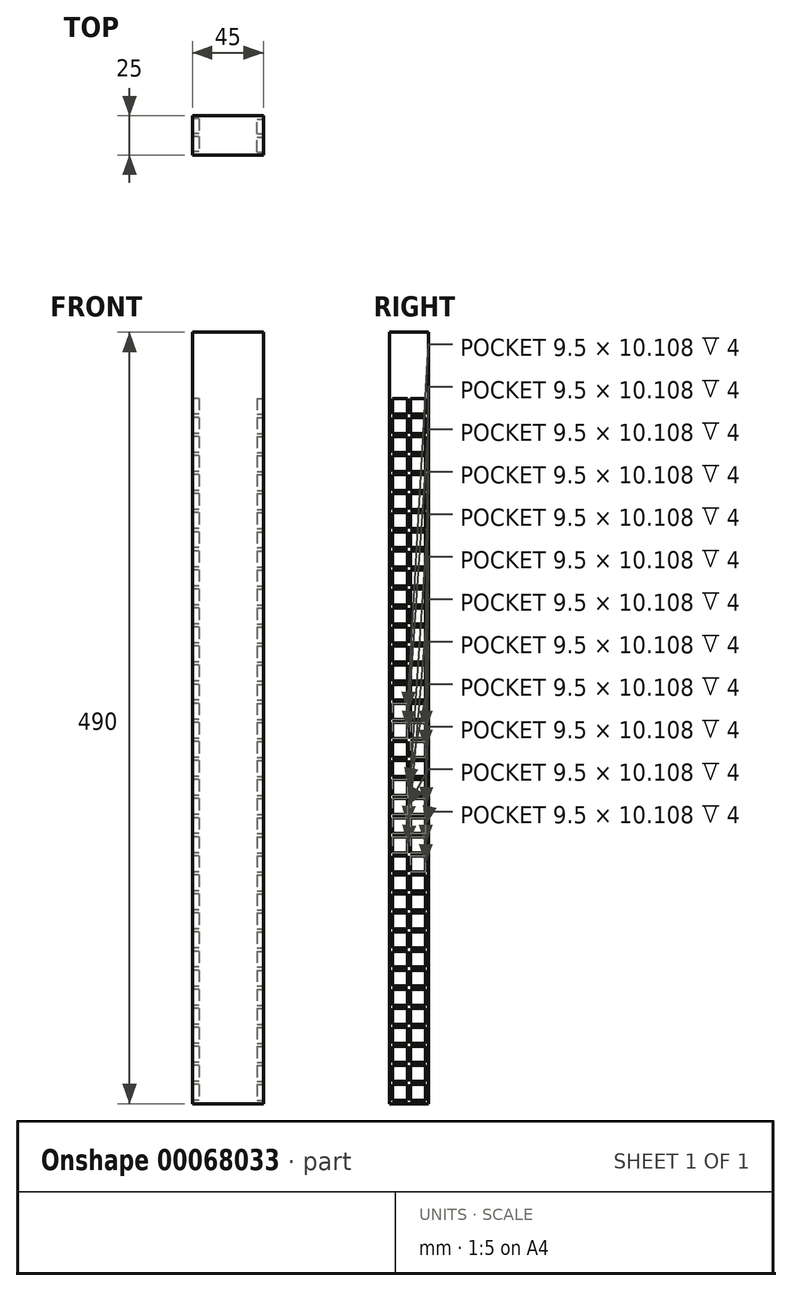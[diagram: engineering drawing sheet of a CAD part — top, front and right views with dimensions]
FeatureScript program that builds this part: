
annotation { "Feature Type Name" : "Feature", "Feature Type Description" : "" }
export const myFeature = defineFeature(function(context is Context, id is Id, definition is map)
    precondition{}
    {
        {
            var Q0;
            Q0=qCreatedBy(makeId("Top.planeOp"),FACE);
            var sketch = newSketch(context, id + "F0", { "sketchPlane" : qUnion([Q0])});
            skLineSegment(sketch, "E0.bottom", {"start": v(0, 0) * mm, "end": v(45, 0) * mm});
            skLineSegment(sketch, "E0.top", {"start": v(0, -25) * mm, "end": v(45, -25) * mm});
            skLineSegment(sketch, "E0.left", {"start": v(0, 0) * mm, "end": v(0, -25) * mm});
            skLineSegment(sketch, "E0.right", {"start": v(45, 0) * mm, "end": v(45, -25) * mm});
            skSolve(sketch);
        }
        {
            var Q0;
            Q0 = qSketchRegion(id + "F0", true);
            extrude(context, id + "F1", {"entities" : qUnion([Q0]), "depth" : 490 * mm});
        }
        {
            var Q0;
            Q0=makeQuery(id+"F1.opExtrude","SWEPT_FACE",FACE,{"disambiguationData":[OSD([sQuery(id+"F0.wireOp",EDGE,"E0.right")])]});
            var sketch = newSketch(context, id + "F2", { "sketchPlane" : qUnion([Q0])});
            skLineSegment(sketch, "E1.bottom", {"start": v(-23, 448) * mm, "end": v(-13.5, 448) * mm});
            skLineSegment(sketch, "E1.top", {"start": v(-23, 437.9) * mm, "end": v(-13.5, 437.9) * mm});
            skLineSegment(sketch, "E1.left", {"start": v(-23, 448) * mm, "end": v(-23, 437.9) * mm});
            skLineSegment(sketch, "E1.right", {"start": v(-13.5, 448) * mm, "end": v(-13.5, 437.9) * mm});
            skLineSegment(sketch, "E2.bottom", {"start": v(-11.5, 448) * mm, "end": v(-2, 448) * mm});
            skLineSegment(sketch, "E2.top", {"start": v(-11.5, 437.9) * mm, "end": v(-2, 437.9) * mm});
            skLineSegment(sketch, "E2.left", {"start": v(-11.5, 448) * mm, "end": v(-11.5, 437.9) * mm});
            skLineSegment(sketch, "E2.right", {"start": v(-2, 448) * mm, "end": v(-2, 437.9) * mm});
            skLineSegment(sketch, "E3.0.1.0", {"start": v(-2, 435.9) * mm, "end": v(-2, 425.78) * mm});
            skLineSegment(sketch, "E3.0.1.1", {"start": v(-11.5, 425.78) * mm, "end": v(-2, 425.78) * mm});
            skLineSegment(sketch, "E3.0.1.2", {"start": v(-23, 425.78) * mm, "end": v(-13.5, 425.78) * mm});
            skLineSegment(sketch, "E3.0.1.3", {"start": v(-23, 435.9) * mm, "end": v(-13.5, 435.9) * mm});
            skLineSegment(sketch, "E3.0.1.4", {"start": v(-23, 435.9) * mm, "end": v(-23, 425.78) * mm});
            skLineSegment(sketch, "E3.0.1.5", {"start": v(-13.5, 435.9) * mm, "end": v(-13.5, 425.78) * mm});
            skLineSegment(sketch, "E3.0.1.6", {"start": v(-11.5, 435.9) * mm, "end": v(-2, 435.9) * mm});
            skLineSegment(sketch, "E3.0.1.7", {"start": v(-11.5, 435.9) * mm, "end": v(-11.5, 425.78) * mm});
            skLineSegment(sketch, "E3.0.2.0", {"start": v(-2, 423.78) * mm, "end": v(-2, 413.68) * mm});
            skLineSegment(sketch, "E3.0.2.1", {"start": v(-11.5, 413.68) * mm, "end": v(-2, 413.68) * mm});
            skLineSegment(sketch, "E3.0.2.2", {"start": v(-23, 413.68) * mm, "end": v(-13.5, 413.68) * mm});
            skLineSegment(sketch, "E3.0.2.3", {"start": v(-23, 423.78) * mm, "end": v(-13.5, 423.78) * mm});
            skLineSegment(sketch, "E3.0.2.4", {"start": v(-23, 423.78) * mm, "end": v(-23, 413.68) * mm});
            skLineSegment(sketch, "E3.0.2.5", {"start": v(-13.5, 423.78) * mm, "end": v(-13.5, 413.68) * mm});
            skLineSegment(sketch, "E3.0.2.6", {"start": v(-11.5, 423.78) * mm, "end": v(-2, 423.78) * mm});
            skLineSegment(sketch, "E3.0.2.7", {"start": v(-11.5, 423.78) * mm, "end": v(-11.5, 413.68) * mm});
            skLineSegment(sketch, "E3.0.3.0", {"start": v(-2, 411.68) * mm, "end": v(-2, 401.57) * mm});
            skLineSegment(sketch, "E3.0.3.1", {"start": v(-11.5, 401.57) * mm, "end": v(-2, 401.57) * mm});
            skLineSegment(sketch, "E3.0.3.2", {"start": v(-23, 401.57) * mm, "end": v(-13.5, 401.57) * mm});
            skLineSegment(sketch, "E3.0.3.3", {"start": v(-23, 411.68) * mm, "end": v(-13.5, 411.68) * mm});
            skLineSegment(sketch, "E3.0.3.4", {"start": v(-23, 411.68) * mm, "end": v(-23, 401.57) * mm});
            skLineSegment(sketch, "E3.0.3.5", {"start": v(-13.5, 411.68) * mm, "end": v(-13.5, 401.57) * mm});
            skLineSegment(sketch, "E3.0.3.6", {"start": v(-11.5, 411.68) * mm, "end": v(-2, 411.68) * mm});
            skLineSegment(sketch, "E3.0.3.7", {"start": v(-11.5, 411.68) * mm, "end": v(-11.5, 401.57) * mm});
            skLineSegment(sketch, "E3.0.4.0", {"start": v(-2, 399.57) * mm, "end": v(-2, 389.46) * mm});
            skLineSegment(sketch, "E3.0.4.1", {"start": v(-11.5, 389.46) * mm, "end": v(-2, 389.46) * mm});
            skLineSegment(sketch, "E3.0.4.2", {"start": v(-23, 389.46) * mm, "end": v(-13.5, 389.46) * mm});
            skLineSegment(sketch, "E3.0.4.3", {"start": v(-23, 399.57) * mm, "end": v(-13.5, 399.57) * mm});
            skLineSegment(sketch, "E3.0.4.4", {"start": v(-23, 399.57) * mm, "end": v(-23, 389.46) * mm});
            skLineSegment(sketch, "E3.0.4.5", {"start": v(-13.5, 399.57) * mm, "end": v(-13.5, 389.46) * mm});
            skLineSegment(sketch, "E3.0.4.6", {"start": v(-11.5, 399.57) * mm, "end": v(-2, 399.57) * mm});
            skLineSegment(sketch, "E3.0.4.7", {"start": v(-11.5, 399.57) * mm, "end": v(-11.5, 389.46) * mm});
            skLineSegment(sketch, "E3.0.5.0", {"start": v(-2, 387.46) * mm, "end": v(-2, 377.35) * mm});
            skLineSegment(sketch, "E3.0.5.1", {"start": v(-11.5, 377.35) * mm, "end": v(-2, 377.35) * mm});
            skLineSegment(sketch, "E3.0.5.2", {"start": v(-23, 377.35) * mm, "end": v(-13.5, 377.35) * mm});
            skLineSegment(sketch, "E3.0.5.3", {"start": v(-23, 387.46) * mm, "end": v(-13.5, 387.46) * mm});
            skLineSegment(sketch, "E3.0.5.4", {"start": v(-23, 387.46) * mm, "end": v(-23, 377.35) * mm});
            skLineSegment(sketch, "E3.0.5.5", {"start": v(-13.5, 387.46) * mm, "end": v(-13.5, 377.35) * mm});
            skLineSegment(sketch, "E3.0.5.6", {"start": v(-11.5, 387.46) * mm, "end": v(-2, 387.46) * mm});
            skLineSegment(sketch, "E3.0.5.7", {"start": v(-11.5, 387.46) * mm, "end": v(-11.5, 377.35) * mm});
            skLineSegment(sketch, "E3.0.6.0", {"start": v(-2, 375.35) * mm, "end": v(-2, 365.24) * mm});
            skLineSegment(sketch, "E3.0.6.1", {"start": v(-11.5, 365.24) * mm, "end": v(-2, 365.24) * mm});
            skLineSegment(sketch, "E3.0.6.2", {"start": v(-23, 365.24) * mm, "end": v(-13.5, 365.24) * mm});
            skLineSegment(sketch, "E3.0.6.3", {"start": v(-23, 375.35) * mm, "end": v(-13.5, 375.35) * mm});
            skLineSegment(sketch, "E3.0.6.4", {"start": v(-23, 375.35) * mm, "end": v(-23, 365.24) * mm});
            skLineSegment(sketch, "E3.0.6.5", {"start": v(-13.5, 375.35) * mm, "end": v(-13.5, 365.24) * mm});
            skLineSegment(sketch, "E3.0.6.6", {"start": v(-11.5, 375.35) * mm, "end": v(-2, 375.35) * mm});
            skLineSegment(sketch, "E3.0.6.7", {"start": v(-11.5, 375.35) * mm, "end": v(-11.5, 365.24) * mm});
            skLineSegment(sketch, "E3.0.7.0", {"start": v(-2, 363.24) * mm, "end": v(-2, 353.14) * mm});
            skLineSegment(sketch, "E3.0.7.1", {"start": v(-11.5, 353.14) * mm, "end": v(-2, 353.14) * mm});
            skLineSegment(sketch, "E3.0.7.2", {"start": v(-23, 353.14) * mm, "end": v(-13.5, 353.14) * mm});
            skLineSegment(sketch, "E3.0.7.3", {"start": v(-23, 363.24) * mm, "end": v(-13.5, 363.24) * mm});
            skLineSegment(sketch, "E3.0.7.4", {"start": v(-23, 363.24) * mm, "end": v(-23, 353.14) * mm});
            skLineSegment(sketch, "E3.0.7.5", {"start": v(-13.5, 363.24) * mm, "end": v(-13.5, 353.14) * mm});
            skLineSegment(sketch, "E3.0.7.6", {"start": v(-11.5, 363.24) * mm, "end": v(-2, 363.24) * mm});
            skLineSegment(sketch, "E3.0.7.7", {"start": v(-11.5, 363.24) * mm, "end": v(-11.5, 353.14) * mm});
            skLineSegment(sketch, "E3.0.8.0", {"start": v(-2, 351.14) * mm, "end": v(-2, 341.03) * mm});
            skLineSegment(sketch, "E3.0.8.1", {"start": v(-11.5, 341.03) * mm, "end": v(-2, 341.03) * mm});
            skLineSegment(sketch, "E3.0.8.2", {"start": v(-23, 341.03) * mm, "end": v(-13.5, 341.03) * mm});
            skLineSegment(sketch, "E3.0.8.3", {"start": v(-23, 351.14) * mm, "end": v(-13.5, 351.14) * mm});
            skLineSegment(sketch, "E3.0.8.4", {"start": v(-23, 351.14) * mm, "end": v(-23, 341.03) * mm});
            skLineSegment(sketch, "E3.0.8.5", {"start": v(-13.5, 351.14) * mm, "end": v(-13.5, 341.03) * mm});
            skLineSegment(sketch, "E3.0.8.6", {"start": v(-11.5, 351.14) * mm, "end": v(-2, 351.14) * mm});
            skLineSegment(sketch, "E3.0.8.7", {"start": v(-11.5, 351.14) * mm, "end": v(-11.5, 341.03) * mm});
            skLineSegment(sketch, "E3.0.9.0", {"start": v(-2, 339.03) * mm, "end": v(-2, 328.92) * mm});
            skLineSegment(sketch, "E3.0.9.1", {"start": v(-11.5, 328.92) * mm, "end": v(-2, 328.92) * mm});
            skLineSegment(sketch, "E3.0.9.2", {"start": v(-23, 328.92) * mm, "end": v(-13.5, 328.92) * mm});
            skLineSegment(sketch, "E3.0.9.3", {"start": v(-23, 339.03) * mm, "end": v(-13.5, 339.03) * mm});
            skLineSegment(sketch, "E3.0.9.4", {"start": v(-23, 339.03) * mm, "end": v(-23, 328.92) * mm});
            skLineSegment(sketch, "E3.0.9.5", {"start": v(-13.5, 339.03) * mm, "end": v(-13.5, 328.92) * mm});
            skLineSegment(sketch, "E3.0.9.6", {"start": v(-11.5, 339.03) * mm, "end": v(-2, 339.03) * mm});
            skLineSegment(sketch, "E3.0.9.7", {"start": v(-11.5, 339.03) * mm, "end": v(-11.5, 328.92) * mm});
            skLineSegment(sketch, "E3.0.10.0", {"start": v(-2, 326.92) * mm, "end": v(-2, 316.81) * mm});
            skLineSegment(sketch, "E3.0.10.1", {"start": v(-11.5, 316.81) * mm, "end": v(-2, 316.81) * mm});
            skLineSegment(sketch, "E3.0.10.2", {"start": v(-23, 316.81) * mm, "end": v(-13.5, 316.81) * mm});
            skLineSegment(sketch, "E3.0.10.3", {"start": v(-23, 326.92) * mm, "end": v(-13.5, 326.92) * mm});
            skLineSegment(sketch, "E3.0.10.4", {"start": v(-23, 326.92) * mm, "end": v(-23, 316.81) * mm});
            skLineSegment(sketch, "E3.0.10.5", {"start": v(-13.5, 326.92) * mm, "end": v(-13.5, 316.81) * mm});
            skLineSegment(sketch, "E3.0.10.6", {"start": v(-11.5, 326.92) * mm, "end": v(-2, 326.92) * mm});
            skLineSegment(sketch, "E3.0.10.7", {"start": v(-11.5, 326.92) * mm, "end": v(-11.5, 316.81) * mm});
            skLineSegment(sketch, "E3.0.11.0", {"start": v(-2, 314.81) * mm, "end": v(-2, 304.7) * mm});
            skLineSegment(sketch, "E3.0.11.1", {"start": v(-11.5, 304.7) * mm, "end": v(-2, 304.7) * mm});
            skLineSegment(sketch, "E3.0.11.2", {"start": v(-23, 304.7) * mm, "end": v(-13.5, 304.7) * mm});
            skLineSegment(sketch, "E3.0.11.3", {"start": v(-23, 314.81) * mm, "end": v(-13.5, 314.81) * mm});
            skLineSegment(sketch, "E3.0.11.4", {"start": v(-23, 314.81) * mm, "end": v(-23, 304.7) * mm});
            skLineSegment(sketch, "E3.0.11.5", {"start": v(-13.5, 314.81) * mm, "end": v(-13.5, 304.7) * mm});
            skLineSegment(sketch, "E3.0.11.6", {"start": v(-11.5, 314.81) * mm, "end": v(-2, 314.81) * mm});
            skLineSegment(sketch, "E3.0.11.7", {"start": v(-11.5, 314.81) * mm, "end": v(-11.5, 304.7) * mm});
            skLineSegment(sketch, "E3.0.12.0", {"start": v(-2, 302.7) * mm, "end": v(-2, 292.6) * mm});
            skLineSegment(sketch, "E3.0.12.1", {"start": v(-11.5, 292.6) * mm, "end": v(-2, 292.6) * mm});
            skLineSegment(sketch, "E3.0.12.2", {"start": v(-23, 292.6) * mm, "end": v(-13.5, 292.6) * mm});
            skLineSegment(sketch, "E3.0.12.3", {"start": v(-23, 302.7) * mm, "end": v(-13.5, 302.7) * mm});
            skLineSegment(sketch, "E3.0.12.4", {"start": v(-23, 302.7) * mm, "end": v(-23, 292.6) * mm});
            skLineSegment(sketch, "E3.0.12.5", {"start": v(-13.5, 302.7) * mm, "end": v(-13.5, 292.6) * mm});
            skLineSegment(sketch, "E3.0.12.6", {"start": v(-11.5, 302.7) * mm, "end": v(-2, 302.7) * mm});
            skLineSegment(sketch, "E3.0.12.7", {"start": v(-11.5, 302.7) * mm, "end": v(-11.5, 292.6) * mm});
            skLineSegment(sketch, "E3.0.13.0", {"start": v(-2, 290.6) * mm, "end": v(-2, 280.49) * mm});
            skLineSegment(sketch, "E3.0.13.1", {"start": v(-11.5, 280.49) * mm, "end": v(-2, 280.49) * mm});
            skLineSegment(sketch, "E3.0.13.2", {"start": v(-23, 280.49) * mm, "end": v(-13.5, 280.49) * mm});
            skLineSegment(sketch, "E3.0.13.3", {"start": v(-23, 290.6) * mm, "end": v(-13.5, 290.6) * mm});
            skLineSegment(sketch, "E3.0.13.4", {"start": v(-23, 290.6) * mm, "end": v(-23, 280.49) * mm});
            skLineSegment(sketch, "E3.0.13.5", {"start": v(-13.5, 290.6) * mm, "end": v(-13.5, 280.49) * mm});
            skLineSegment(sketch, "E3.0.13.6", {"start": v(-11.5, 290.6) * mm, "end": v(-2, 290.6) * mm});
            skLineSegment(sketch, "E3.0.13.7", {"start": v(-11.5, 290.6) * mm, "end": v(-11.5, 280.49) * mm});
            skLineSegment(sketch, "E3.0.14.0", {"start": v(-2, 278.49) * mm, "end": v(-2, 268.38) * mm});
            skLineSegment(sketch, "E3.0.14.1", {"start": v(-11.5, 268.38) * mm, "end": v(-2, 268.38) * mm});
            skLineSegment(sketch, "E3.0.14.2", {"start": v(-23, 268.38) * mm, "end": v(-13.5, 268.38) * mm});
            skLineSegment(sketch, "E3.0.14.3", {"start": v(-23, 278.49) * mm, "end": v(-13.5, 278.49) * mm});
            skLineSegment(sketch, "E3.0.14.4", {"start": v(-23, 278.49) * mm, "end": v(-23, 268.38) * mm});
            skLineSegment(sketch, "E3.0.14.5", {"start": v(-13.5, 278.49) * mm, "end": v(-13.5, 268.38) * mm});
            skLineSegment(sketch, "E3.0.14.6", {"start": v(-11.5, 278.49) * mm, "end": v(-2, 278.49) * mm});
            skLineSegment(sketch, "E3.0.14.7", {"start": v(-11.5, 278.49) * mm, "end": v(-11.5, 268.38) * mm});
            skLineSegment(sketch, "E3.0.15.0", {"start": v(-2, 266.38) * mm, "end": v(-2, 256.27) * mm});
            skLineSegment(sketch, "E3.0.15.1", {"start": v(-11.5, 256.27) * mm, "end": v(-2, 256.27) * mm});
            skLineSegment(sketch, "E3.0.15.2", {"start": v(-23, 256.27) * mm, "end": v(-13.5, 256.27) * mm});
            skLineSegment(sketch, "E3.0.15.3", {"start": v(-23, 266.38) * mm, "end": v(-13.5, 266.38) * mm});
            skLineSegment(sketch, "E3.0.15.4", {"start": v(-23, 266.38) * mm, "end": v(-23, 256.27) * mm});
            skLineSegment(sketch, "E3.0.15.5", {"start": v(-13.5, 266.38) * mm, "end": v(-13.5, 256.27) * mm});
            skLineSegment(sketch, "E3.0.15.6", {"start": v(-11.5, 266.38) * mm, "end": v(-2, 266.38) * mm});
            skLineSegment(sketch, "E3.0.15.7", {"start": v(-11.5, 266.38) * mm, "end": v(-11.5, 256.27) * mm});
            skLineSegment(sketch, "E3.0.16.0", {"start": v(-2, 254.27) * mm, "end": v(-2, 244.16) * mm});
            skLineSegment(sketch, "E3.0.16.1", {"start": v(-11.5, 244.16) * mm, "end": v(-2, 244.16) * mm});
            skLineSegment(sketch, "E3.0.16.2", {"start": v(-23, 244.16) * mm, "end": v(-13.5, 244.16) * mm});
            skLineSegment(sketch, "E3.0.16.3", {"start": v(-23, 254.27) * mm, "end": v(-13.5, 254.27) * mm});
            skLineSegment(sketch, "E3.0.16.4", {"start": v(-23, 254.27) * mm, "end": v(-23, 244.16) * mm});
            skLineSegment(sketch, "E3.0.16.5", {"start": v(-13.5, 254.27) * mm, "end": v(-13.5, 244.16) * mm});
            skLineSegment(sketch, "E3.0.16.6", {"start": v(-11.5, 254.27) * mm, "end": v(-2, 254.27) * mm});
            skLineSegment(sketch, "E3.0.16.7", {"start": v(-11.5, 254.27) * mm, "end": v(-11.5, 244.16) * mm});
            skLineSegment(sketch, "E3.0.17.0", {"start": v(-2, 242.16) * mm, "end": v(-2, 232.06) * mm});
            skLineSegment(sketch, "E3.0.17.1", {"start": v(-11.5, 232.06) * mm, "end": v(-2, 232.06) * mm});
            skLineSegment(sketch, "E3.0.17.2", {"start": v(-23, 232.06) * mm, "end": v(-13.5, 232.06) * mm});
            skLineSegment(sketch, "E3.0.17.3", {"start": v(-23, 242.16) * mm, "end": v(-13.5, 242.16) * mm});
            skLineSegment(sketch, "E3.0.17.4", {"start": v(-23, 242.16) * mm, "end": v(-23, 232.06) * mm});
            skLineSegment(sketch, "E3.0.17.5", {"start": v(-13.5, 242.16) * mm, "end": v(-13.5, 232.06) * mm});
            skLineSegment(sketch, "E3.0.17.6", {"start": v(-11.5, 242.16) * mm, "end": v(-2, 242.16) * mm});
            skLineSegment(sketch, "E3.0.17.7", {"start": v(-11.5, 242.16) * mm, "end": v(-11.5, 232.06) * mm});
            skLineSegment(sketch, "E3.0.18.0", {"start": v(-2, 230.06) * mm, "end": v(-2, 219.95) * mm});
            skLineSegment(sketch, "E3.0.18.1", {"start": v(-11.5, 219.95) * mm, "end": v(-2, 219.95) * mm});
            skLineSegment(sketch, "E3.0.18.2", {"start": v(-23, 219.95) * mm, "end": v(-13.5, 219.95) * mm});
            skLineSegment(sketch, "E3.0.18.3", {"start": v(-23, 230.06) * mm, "end": v(-13.5, 230.06) * mm});
            skLineSegment(sketch, "E3.0.18.4", {"start": v(-23, 230.06) * mm, "end": v(-23, 219.95) * mm});
            skLineSegment(sketch, "E3.0.18.5", {"start": v(-13.5, 230.06) * mm, "end": v(-13.5, 219.95) * mm});
            skLineSegment(sketch, "E3.0.18.6", {"start": v(-11.5, 230.06) * mm, "end": v(-2, 230.06) * mm});
            skLineSegment(sketch, "E3.0.18.7", {"start": v(-11.5, 230.06) * mm, "end": v(-11.5, 219.95) * mm});
            skLineSegment(sketch, "E3.0.19.0", {"start": v(-2, 217.95) * mm, "end": v(-2, 207.84) * mm});
            skLineSegment(sketch, "E3.0.19.1", {"start": v(-11.5, 207.84) * mm, "end": v(-2, 207.84) * mm});
            skLineSegment(sketch, "E3.0.19.2", {"start": v(-23, 207.84) * mm, "end": v(-13.5, 207.84) * mm});
            skLineSegment(sketch, "E3.0.19.3", {"start": v(-23, 217.95) * mm, "end": v(-13.5, 217.95) * mm});
            skLineSegment(sketch, "E3.0.19.4", {"start": v(-23, 217.95) * mm, "end": v(-23, 207.84) * mm});
            skLineSegment(sketch, "E3.0.19.5", {"start": v(-13.5, 217.95) * mm, "end": v(-13.5, 207.84) * mm});
            skLineSegment(sketch, "E3.0.19.6", {"start": v(-11.5, 217.95) * mm, "end": v(-2, 217.95) * mm});
            skLineSegment(sketch, "E3.0.19.7", {"start": v(-11.5, 217.95) * mm, "end": v(-11.5, 207.84) * mm});
            skLineSegment(sketch, "E3.0.20.0", {"start": v(-2, 205.84) * mm, "end": v(-2, 195.73) * mm});
            skLineSegment(sketch, "E3.0.20.1", {"start": v(-11.5, 195.73) * mm, "end": v(-2, 195.73) * mm});
            skLineSegment(sketch, "E3.0.20.2", {"start": v(-23, 195.73) * mm, "end": v(-13.5, 195.73) * mm});
            skLineSegment(sketch, "E3.0.20.3", {"start": v(-23, 205.84) * mm, "end": v(-13.5, 205.84) * mm});
            skLineSegment(sketch, "E3.0.20.4", {"start": v(-23, 205.84) * mm, "end": v(-23, 195.73) * mm});
            skLineSegment(sketch, "E3.0.20.5", {"start": v(-13.5, 205.84) * mm, "end": v(-13.5, 195.73) * mm});
            skLineSegment(sketch, "E3.0.20.6", {"start": v(-11.5, 205.84) * mm, "end": v(-2, 205.84) * mm});
            skLineSegment(sketch, "E3.0.20.7", {"start": v(-11.5, 205.84) * mm, "end": v(-11.5, 195.73) * mm});
            skLineSegment(sketch, "E3.0.21.0", {"start": v(-2, 193.73) * mm, "end": v(-2, 183.62) * mm});
            skLineSegment(sketch, "E3.0.21.1", {"start": v(-11.5, 183.62) * mm, "end": v(-2, 183.62) * mm});
            skLineSegment(sketch, "E3.0.21.2", {"start": v(-23, 183.62) * mm, "end": v(-13.5, 183.62) * mm});
            skLineSegment(sketch, "E3.0.21.3", {"start": v(-23, 193.73) * mm, "end": v(-13.5, 193.73) * mm});
            skLineSegment(sketch, "E3.0.21.4", {"start": v(-23, 193.73) * mm, "end": v(-23, 183.62) * mm});
            skLineSegment(sketch, "E3.0.21.5", {"start": v(-13.5, 193.73) * mm, "end": v(-13.5, 183.62) * mm});
            skLineSegment(sketch, "E3.0.21.6", {"start": v(-11.5, 193.73) * mm, "end": v(-2, 193.73) * mm});
            skLineSegment(sketch, "E3.0.21.7", {"start": v(-11.5, 193.73) * mm, "end": v(-11.5, 183.62) * mm});
            skLineSegment(sketch, "E3.0.22.0", {"start": v(-2, 181.62) * mm, "end": v(-2, 171.52) * mm});
            skLineSegment(sketch, "E3.0.22.1", {"start": v(-11.5, 171.52) * mm, "end": v(-2, 171.52) * mm});
            skLineSegment(sketch, "E3.0.22.2", {"start": v(-23, 171.52) * mm, "end": v(-13.5, 171.52) * mm});
            skLineSegment(sketch, "E3.0.22.3", {"start": v(-23, 181.62) * mm, "end": v(-13.5, 181.62) * mm});
            skLineSegment(sketch, "E3.0.22.4", {"start": v(-23, 181.62) * mm, "end": v(-23, 171.52) * mm});
            skLineSegment(sketch, "E3.0.22.5", {"start": v(-13.5, 181.62) * mm, "end": v(-13.5, 171.52) * mm});
            skLineSegment(sketch, "E3.0.22.6", {"start": v(-11.5, 181.62) * mm, "end": v(-2, 181.62) * mm});
            skLineSegment(sketch, "E3.0.22.7", {"start": v(-11.5, 181.62) * mm, "end": v(-11.5, 171.52) * mm});
            skLineSegment(sketch, "E3.0.23.0", {"start": v(-2, 169.52) * mm, "end": v(-2, 159.4) * mm});
            skLineSegment(sketch, "E3.0.23.1", {"start": v(-11.5, 159.4) * mm, "end": v(-2, 159.4) * mm});
            skLineSegment(sketch, "E3.0.23.2", {"start": v(-23, 159.4) * mm, "end": v(-13.5, 159.4) * mm});
            skLineSegment(sketch, "E3.0.23.3", {"start": v(-23, 169.52) * mm, "end": v(-13.5, 169.52) * mm});
            skLineSegment(sketch, "E3.0.23.4", {"start": v(-23, 169.52) * mm, "end": v(-23, 159.4) * mm});
            skLineSegment(sketch, "E3.0.23.5", {"start": v(-13.5, 169.52) * mm, "end": v(-13.5, 159.4) * mm});
            skLineSegment(sketch, "E3.0.23.6", {"start": v(-11.5, 169.52) * mm, "end": v(-2, 169.52) * mm});
            skLineSegment(sketch, "E3.0.23.7", {"start": v(-11.5, 169.52) * mm, "end": v(-11.5, 159.4) * mm});
            skLineSegment(sketch, "E3.0.24.0", {"start": v(-2, 157.4) * mm, "end": v(-2, 147.3) * mm});
            skLineSegment(sketch, "E3.0.24.1", {"start": v(-11.5, 147.3) * mm, "end": v(-2, 147.3) * mm});
            skLineSegment(sketch, "E3.0.24.2", {"start": v(-23, 147.3) * mm, "end": v(-13.5, 147.3) * mm});
            skLineSegment(sketch, "E3.0.24.3", {"start": v(-23, 157.4) * mm, "end": v(-13.5, 157.4) * mm});
            skLineSegment(sketch, "E3.0.24.4", {"start": v(-23, 157.4) * mm, "end": v(-23, 147.3) * mm});
            skLineSegment(sketch, "E3.0.24.5", {"start": v(-13.5, 157.4) * mm, "end": v(-13.5, 147.3) * mm});
            skLineSegment(sketch, "E3.0.24.6", {"start": v(-11.5, 157.4) * mm, "end": v(-2, 157.4) * mm});
            skLineSegment(sketch, "E3.0.24.7", {"start": v(-11.5, 157.4) * mm, "end": v(-11.5, 147.3) * mm});
            skLineSegment(sketch, "E3.0.25.0", {"start": v(-2, 145.3) * mm, "end": v(-2, 135.2) * mm});
            skLineSegment(sketch, "E3.0.25.1", {"start": v(-11.5, 135.2) * mm, "end": v(-2, 135.2) * mm});
            skLineSegment(sketch, "E3.0.25.2", {"start": v(-23, 135.2) * mm, "end": v(-13.5, 135.2) * mm});
            skLineSegment(sketch, "E3.0.25.3", {"start": v(-23, 145.3) * mm, "end": v(-13.5, 145.3) * mm});
            skLineSegment(sketch, "E3.0.25.4", {"start": v(-23, 145.3) * mm, "end": v(-23, 135.2) * mm});
            skLineSegment(sketch, "E3.0.25.5", {"start": v(-13.5, 145.3) * mm, "end": v(-13.5, 135.2) * mm});
            skLineSegment(sketch, "E3.0.25.6", {"start": v(-11.5, 145.3) * mm, "end": v(-2, 145.3) * mm});
            skLineSegment(sketch, "E3.0.25.7", {"start": v(-11.5, 145.3) * mm, "end": v(-11.5, 135.2) * mm});
            skLineSegment(sketch, "E3.0.26.0", {"start": v(-2, 133.2) * mm, "end": v(-2, 123.08) * mm});
            skLineSegment(sketch, "E3.0.26.1", {"start": v(-11.5, 123.08) * mm, "end": v(-2, 123.08) * mm});
            skLineSegment(sketch, "E3.0.26.2", {"start": v(-23, 123.08) * mm, "end": v(-13.5, 123.08) * mm});
            skLineSegment(sketch, "E3.0.26.3", {"start": v(-23, 133.2) * mm, "end": v(-13.5, 133.2) * mm});
            skLineSegment(sketch, "E3.0.26.4", {"start": v(-23, 133.2) * mm, "end": v(-23, 123.08) * mm});
            skLineSegment(sketch, "E3.0.26.5", {"start": v(-13.5, 133.2) * mm, "end": v(-13.5, 123.08) * mm});
            skLineSegment(sketch, "E3.0.26.6", {"start": v(-11.5, 133.2) * mm, "end": v(-2, 133.2) * mm});
            skLineSegment(sketch, "E3.0.26.7", {"start": v(-11.5, 133.2) * mm, "end": v(-11.5, 123.08) * mm});
            skLineSegment(sketch, "E3.0.27.0", {"start": v(-2, 121.08) * mm, "end": v(-2, 110.98) * mm});
            skLineSegment(sketch, "E3.0.27.1", {"start": v(-11.5, 110.98) * mm, "end": v(-2, 110.98) * mm});
            skLineSegment(sketch, "E3.0.27.2", {"start": v(-23, 110.98) * mm, "end": v(-13.5, 110.98) * mm});
            skLineSegment(sketch, "E3.0.27.3", {"start": v(-23, 121.08) * mm, "end": v(-13.5, 121.08) * mm});
            skLineSegment(sketch, "E3.0.27.4", {"start": v(-23, 121.08) * mm, "end": v(-23, 110.98) * mm});
            skLineSegment(sketch, "E3.0.27.5", {"start": v(-13.5, 121.08) * mm, "end": v(-13.5, 110.98) * mm});
            skLineSegment(sketch, "E3.0.27.6", {"start": v(-11.5, 121.08) * mm, "end": v(-2, 121.08) * mm});
            skLineSegment(sketch, "E3.0.27.7", {"start": v(-11.5, 121.08) * mm, "end": v(-11.5, 110.98) * mm});
            skLineSegment(sketch, "E3.0.28.0", {"start": v(-2, 108.98) * mm, "end": v(-2, 98.87) * mm});
            skLineSegment(sketch, "E3.0.28.1", {"start": v(-11.5, 98.87) * mm, "end": v(-2, 98.87) * mm});
            skLineSegment(sketch, "E3.0.28.2", {"start": v(-23, 98.87) * mm, "end": v(-13.5, 98.87) * mm});
            skLineSegment(sketch, "E3.0.28.3", {"start": v(-23, 108.98) * mm, "end": v(-13.5, 108.98) * mm});
            skLineSegment(sketch, "E3.0.28.4", {"start": v(-23, 108.98) * mm, "end": v(-23, 98.87) * mm});
            skLineSegment(sketch, "E3.0.28.5", {"start": v(-13.5, 108.98) * mm, "end": v(-13.5, 98.87) * mm});
            skLineSegment(sketch, "E3.0.28.6", {"start": v(-11.5, 108.98) * mm, "end": v(-2, 108.98) * mm});
            skLineSegment(sketch, "E3.0.28.7", {"start": v(-11.5, 108.98) * mm, "end": v(-11.5, 98.87) * mm});
            skLineSegment(sketch, "E3.0.29.0", {"start": v(-2, 96.87) * mm, "end": v(-2, 86.76) * mm});
            skLineSegment(sketch, "E3.0.29.1", {"start": v(-11.5, 86.76) * mm, "end": v(-2, 86.76) * mm});
            skLineSegment(sketch, "E3.0.29.2", {"start": v(-23, 86.76) * mm, "end": v(-13.5, 86.76) * mm});
            skLineSegment(sketch, "E3.0.29.3", {"start": v(-23, 96.87) * mm, "end": v(-13.5, 96.87) * mm});
            skLineSegment(sketch, "E3.0.29.4", {"start": v(-23, 96.87) * mm, "end": v(-23, 86.76) * mm});
            skLineSegment(sketch, "E3.0.29.5", {"start": v(-13.5, 96.87) * mm, "end": v(-13.5, 86.76) * mm});
            skLineSegment(sketch, "E3.0.29.6", {"start": v(-11.5, 96.87) * mm, "end": v(-2, 96.87) * mm});
            skLineSegment(sketch, "E3.0.29.7", {"start": v(-11.5, 96.87) * mm, "end": v(-11.5, 86.76) * mm});
            skLineSegment(sketch, "E3.0.30.0", {"start": v(-2, 84.76) * mm, "end": v(-2, 74.65) * mm});
            skLineSegment(sketch, "E3.0.30.1", {"start": v(-11.5, 74.65) * mm, "end": v(-2, 74.65) * mm});
            skLineSegment(sketch, "E3.0.30.2", {"start": v(-23, 74.65) * mm, "end": v(-13.5, 74.65) * mm});
            skLineSegment(sketch, "E3.0.30.3", {"start": v(-23, 84.76) * mm, "end": v(-13.5, 84.76) * mm});
            skLineSegment(sketch, "E3.0.30.4", {"start": v(-23, 84.76) * mm, "end": v(-23, 74.65) * mm});
            skLineSegment(sketch, "E3.0.30.5", {"start": v(-13.5, 84.76) * mm, "end": v(-13.5, 74.65) * mm});
            skLineSegment(sketch, "E3.0.30.6", {"start": v(-11.5, 84.76) * mm, "end": v(-2, 84.76) * mm});
            skLineSegment(sketch, "E3.0.30.7", {"start": v(-11.5, 84.76) * mm, "end": v(-11.5, 74.65) * mm});
            skLineSegment(sketch, "E3.0.31.0", {"start": v(-2, 72.65) * mm, "end": v(-2, 62.54) * mm});
            skLineSegment(sketch, "E3.0.31.1", {"start": v(-11.5, 62.54) * mm, "end": v(-2, 62.54) * mm});
            skLineSegment(sketch, "E3.0.31.2", {"start": v(-23, 62.54) * mm, "end": v(-13.5, 62.54) * mm});
            skLineSegment(sketch, "E3.0.31.3", {"start": v(-23, 72.65) * mm, "end": v(-13.5, 72.65) * mm});
            skLineSegment(sketch, "E3.0.31.4", {"start": v(-23, 72.65) * mm, "end": v(-23, 62.54) * mm});
            skLineSegment(sketch, "E3.0.31.5", {"start": v(-13.5, 72.65) * mm, "end": v(-13.5, 62.54) * mm});
            skLineSegment(sketch, "E3.0.31.6", {"start": v(-11.5, 72.65) * mm, "end": v(-2, 72.65) * mm});
            skLineSegment(sketch, "E3.0.31.7", {"start": v(-11.5, 72.65) * mm, "end": v(-11.5, 62.54) * mm});
            skLineSegment(sketch, "E3.0.32.0", {"start": v(-2, 60.54) * mm, "end": v(-2, 50.44) * mm});
            skLineSegment(sketch, "E3.0.32.1", {"start": v(-11.5, 50.44) * mm, "end": v(-2, 50.44) * mm});
            skLineSegment(sketch, "E3.0.32.2", {"start": v(-23, 50.44) * mm, "end": v(-13.5, 50.44) * mm});
            skLineSegment(sketch, "E3.0.32.3", {"start": v(-23, 60.54) * mm, "end": v(-13.5, 60.54) * mm});
            skLineSegment(sketch, "E3.0.32.4", {"start": v(-23, 60.54) * mm, "end": v(-23, 50.44) * mm});
            skLineSegment(sketch, "E3.0.32.5", {"start": v(-13.5, 60.54) * mm, "end": v(-13.5, 50.44) * mm});
            skLineSegment(sketch, "E3.0.32.6", {"start": v(-11.5, 60.54) * mm, "end": v(-2, 60.54) * mm});
            skLineSegment(sketch, "E3.0.32.7", {"start": v(-11.5, 60.54) * mm, "end": v(-11.5, 50.44) * mm});
            skLineSegment(sketch, "E3.0.33.0", {"start": v(-2, 48.44) * mm, "end": v(-2, 38.33) * mm});
            skLineSegment(sketch, "E3.0.33.1", {"start": v(-11.5, 38.33) * mm, "end": v(-2, 38.33) * mm});
            skLineSegment(sketch, "E3.0.33.2", {"start": v(-23, 38.33) * mm, "end": v(-13.5, 38.33) * mm});
            skLineSegment(sketch, "E3.0.33.3", {"start": v(-23, 48.44) * mm, "end": v(-13.5, 48.44) * mm});
            skLineSegment(sketch, "E3.0.33.4", {"start": v(-23, 48.44) * mm, "end": v(-23, 38.33) * mm});
            skLineSegment(sketch, "E3.0.33.5", {"start": v(-13.5, 48.44) * mm, "end": v(-13.5, 38.33) * mm});
            skLineSegment(sketch, "E3.0.33.6", {"start": v(-11.5, 48.44) * mm, "end": v(-2, 48.44) * mm});
            skLineSegment(sketch, "E3.0.33.7", {"start": v(-11.5, 48.44) * mm, "end": v(-11.5, 38.33) * mm});
            skLineSegment(sketch, "E3.0.34.0", {"start": v(-2, 36.33) * mm, "end": v(-2, 26.22) * mm});
            skLineSegment(sketch, "E3.0.34.1", {"start": v(-11.5, 26.22) * mm, "end": v(-2, 26.22) * mm});
            skLineSegment(sketch, "E3.0.34.2", {"start": v(-23, 26.22) * mm, "end": v(-13.5, 26.22) * mm});
            skLineSegment(sketch, "E3.0.34.3", {"start": v(-23, 36.33) * mm, "end": v(-13.5, 36.33) * mm});
            skLineSegment(sketch, "E3.0.34.4", {"start": v(-23, 36.33) * mm, "end": v(-23, 26.22) * mm});
            skLineSegment(sketch, "E3.0.34.5", {"start": v(-13.5, 36.33) * mm, "end": v(-13.5, 26.22) * mm});
            skLineSegment(sketch, "E3.0.34.6", {"start": v(-11.5, 36.33) * mm, "end": v(-2, 36.33) * mm});
            skLineSegment(sketch, "E3.0.34.7", {"start": v(-11.5, 36.33) * mm, "end": v(-11.5, 26.22) * mm});
            skLineSegment(sketch, "E3.0.35.0", {"start": v(-2, 24.22) * mm, "end": v(-2, 14.11) * mm});
            skLineSegment(sketch, "E3.0.35.1", {"start": v(-11.5, 14.11) * mm, "end": v(-2, 14.11) * mm});
            skLineSegment(sketch, "E3.0.35.2", {"start": v(-23, 14.11) * mm, "end": v(-13.5, 14.11) * mm});
            skLineSegment(sketch, "E3.0.35.3", {"start": v(-23, 24.22) * mm, "end": v(-13.5, 24.22) * mm});
            skLineSegment(sketch, "E3.0.35.4", {"start": v(-23, 24.22) * mm, "end": v(-23, 14.11) * mm});
            skLineSegment(sketch, "E3.0.35.5", {"start": v(-13.5, 24.22) * mm, "end": v(-13.5, 14.11) * mm});
            skLineSegment(sketch, "E3.0.35.6", {"start": v(-11.5, 24.22) * mm, "end": v(-2, 24.22) * mm});
            skLineSegment(sketch, "E3.0.35.7", {"start": v(-11.5, 24.22) * mm, "end": v(-11.5, 14.11) * mm});
            skLineSegment(sketch, "E3.0.36.0", {"start": v(-2, 12.11) * mm, "end": v(-2, 2) * mm});
            skLineSegment(sketch, "E3.0.36.1", {"start": v(-11.5, 2) * mm, "end": v(-2, 2) * mm});
            skLineSegment(sketch, "E3.0.36.2", {"start": v(-23, 2) * mm, "end": v(-13.5, 2) * mm});
            skLineSegment(sketch, "E3.0.36.3", {"start": v(-23, 12.11) * mm, "end": v(-13.5, 12.11) * mm});
            skLineSegment(sketch, "E3.0.36.4", {"start": v(-23, 12.11) * mm, "end": v(-23, 2) * mm});
            skLineSegment(sketch, "E3.0.36.5", {"start": v(-13.5, 12.11) * mm, "end": v(-13.5, 2) * mm});
            skLineSegment(sketch, "E3.0.36.6", {"start": v(-11.5, 12.11) * mm, "end": v(-2, 12.11) * mm});
            skLineSegment(sketch, "E3.0.36.7", {"start": v(-11.5, 12.11) * mm, "end": v(-11.5, 2) * mm});
            skLineSegment(sketch, "E3.direction1", {"start": v(-2, 437.9) * mm, "end": v(23, 437.9) * mm, "construction": true});
            skLineSegment(sketch, "E3.direction2", {"start": v(-2, 437.9) * mm, "end": v(-2, 425.78) * mm, "construction": true});
            skSolve(sketch);
        }
        {
            var Q0;
            Q0 = qSketchRegion(id + "F2", true);
            extrude(context, id + "F3", {"entities" : qUnion([Q0]), "operationType" : NewBodyOperationType.REMOVE, "oppositeDirection" : true, "depth" : 4 * mm});
        }
        {
            var Q0;
            Q0=makeQuery(id+"F1.opExtrude","SWEPT_FACE",FACE,{"disambiguationData":[OSD([sQuery(id+"F0.wireOp",EDGE,"E0.left")])]});
            var sketch = newSketch(context, id + "F4", { "sketchPlane" : qUnion([Q0])});
            skLineSegment(sketch, "E4.bottom", {"start": v(1.89, 448) * mm, "end": v(11.39, 448) * mm});
            skLineSegment(sketch, "E4.top", {"start": v(1.89, 437.89) * mm, "end": v(11.39, 437.89) * mm});
            skLineSegment(sketch, "E4.left", {"start": v(1.89, 448) * mm, "end": v(1.89, 437.89) * mm});
            skLineSegment(sketch, "E4.right", {"start": v(11.39, 448) * mm, "end": v(11.39, 437.89) * mm});
            skLineSegment(sketch, "E5.bottom", {"start": v(13.39, 448) * mm, "end": v(22.89, 448) * mm});
            skLineSegment(sketch, "E5.top", {"start": v(13.39, 437.89) * mm, "end": v(22.89, 437.89) * mm});
            skLineSegment(sketch, "E5.left", {"start": v(13.39, 448) * mm, "end": v(13.39, 437.89) * mm});
            skLineSegment(sketch, "E5.right", {"start": v(22.89, 448) * mm, "end": v(22.89, 437.89) * mm});
            skLineSegment(sketch, "E6.0.1.0", {"start": v(22.89, 435.89) * mm, "end": v(22.89, 425.78) * mm});
            skLineSegment(sketch, "E6.0.1.1", {"start": v(13.39, 425.78) * mm, "end": v(22.89, 425.78) * mm});
            skLineSegment(sketch, "E6.0.1.2", {"start": v(1.89, 425.78) * mm, "end": v(11.39, 425.78) * mm});
            skLineSegment(sketch, "E6.0.1.3", {"start": v(1.89, 435.89) * mm, "end": v(11.39, 435.89) * mm});
            skLineSegment(sketch, "E6.0.1.4", {"start": v(1.89, 435.89) * mm, "end": v(1.89, 425.78) * mm});
            skLineSegment(sketch, "E6.0.1.5", {"start": v(11.39, 435.89) * mm, "end": v(11.39, 425.78) * mm});
            skLineSegment(sketch, "E6.0.1.6", {"start": v(13.39, 435.89) * mm, "end": v(22.89, 435.89) * mm});
            skLineSegment(sketch, "E6.0.1.7", {"start": v(13.39, 435.89) * mm, "end": v(13.39, 425.78) * mm});
            skLineSegment(sketch, "E6.0.2.0", {"start": v(22.89, 423.78) * mm, "end": v(22.89, 413.67) * mm});
            skLineSegment(sketch, "E6.0.2.1", {"start": v(13.39, 413.67) * mm, "end": v(22.89, 413.67) * mm});
            skLineSegment(sketch, "E6.0.2.2", {"start": v(1.89, 413.67) * mm, "end": v(11.39, 413.67) * mm});
            skLineSegment(sketch, "E6.0.2.3", {"start": v(1.89, 423.78) * mm, "end": v(11.39, 423.78) * mm});
            skLineSegment(sketch, "E6.0.2.4", {"start": v(1.89, 423.78) * mm, "end": v(1.89, 413.67) * mm});
            skLineSegment(sketch, "E6.0.2.5", {"start": v(11.39, 423.78) * mm, "end": v(11.39, 413.67) * mm});
            skLineSegment(sketch, "E6.0.2.6", {"start": v(13.39, 423.78) * mm, "end": v(22.89, 423.78) * mm});
            skLineSegment(sketch, "E6.0.2.7", {"start": v(13.39, 423.78) * mm, "end": v(13.39, 413.67) * mm});
            skLineSegment(sketch, "E6.0.3.0", {"start": v(22.89, 411.67) * mm, "end": v(22.89, 401.56) * mm});
            skLineSegment(sketch, "E6.0.3.1", {"start": v(13.39, 401.56) * mm, "end": v(22.89, 401.56) * mm});
            skLineSegment(sketch, "E6.0.3.2", {"start": v(1.89, 401.56) * mm, "end": v(11.39, 401.56) * mm});
            skLineSegment(sketch, "E6.0.3.3", {"start": v(1.89, 411.67) * mm, "end": v(11.39, 411.67) * mm});
            skLineSegment(sketch, "E6.0.3.4", {"start": v(1.89, 411.67) * mm, "end": v(1.89, 401.56) * mm});
            skLineSegment(sketch, "E6.0.3.5", {"start": v(11.39, 411.67) * mm, "end": v(11.39, 401.56) * mm});
            skLineSegment(sketch, "E6.0.3.6", {"start": v(13.39, 411.67) * mm, "end": v(22.89, 411.67) * mm});
            skLineSegment(sketch, "E6.0.3.7", {"start": v(13.39, 411.67) * mm, "end": v(13.39, 401.56) * mm});
            skLineSegment(sketch, "E6.0.4.0", {"start": v(22.89, 399.56) * mm, "end": v(22.89, 389.46) * mm});
            skLineSegment(sketch, "E6.0.4.1", {"start": v(13.39, 389.46) * mm, "end": v(22.89, 389.46) * mm});
            skLineSegment(sketch, "E6.0.4.2", {"start": v(1.89, 389.46) * mm, "end": v(11.39, 389.46) * mm});
            skLineSegment(sketch, "E6.0.4.3", {"start": v(1.89, 399.56) * mm, "end": v(11.39, 399.56) * mm});
            skLineSegment(sketch, "E6.0.4.4", {"start": v(1.89, 399.56) * mm, "end": v(1.89, 389.46) * mm});
            skLineSegment(sketch, "E6.0.4.5", {"start": v(11.39, 399.56) * mm, "end": v(11.39, 389.46) * mm});
            skLineSegment(sketch, "E6.0.4.6", {"start": v(13.39, 399.56) * mm, "end": v(22.89, 399.56) * mm});
            skLineSegment(sketch, "E6.0.4.7", {"start": v(13.39, 399.56) * mm, "end": v(13.39, 389.46) * mm});
            skLineSegment(sketch, "E6.0.5.0", {"start": v(22.89, 387.46) * mm, "end": v(22.89, 377.35) * mm});
            skLineSegment(sketch, "E6.0.5.1", {"start": v(13.39, 377.35) * mm, "end": v(22.89, 377.35) * mm});
            skLineSegment(sketch, "E6.0.5.2", {"start": v(1.89, 377.35) * mm, "end": v(11.39, 377.35) * mm});
            skLineSegment(sketch, "E6.0.5.3", {"start": v(1.89, 387.46) * mm, "end": v(11.39, 387.46) * mm});
            skLineSegment(sketch, "E6.0.5.4", {"start": v(1.89, 387.46) * mm, "end": v(1.89, 377.35) * mm});
            skLineSegment(sketch, "E6.0.5.5", {"start": v(11.39, 387.46) * mm, "end": v(11.39, 377.35) * mm});
            skLineSegment(sketch, "E6.0.5.6", {"start": v(13.39, 387.46) * mm, "end": v(22.89, 387.46) * mm});
            skLineSegment(sketch, "E6.0.5.7", {"start": v(13.39, 387.46) * mm, "end": v(13.39, 377.35) * mm});
            skLineSegment(sketch, "E6.0.6.0", {"start": v(22.89, 375.35) * mm, "end": v(22.89, 365.24) * mm});
            skLineSegment(sketch, "E6.0.6.1", {"start": v(13.39, 365.24) * mm, "end": v(22.89, 365.24) * mm});
            skLineSegment(sketch, "E6.0.6.2", {"start": v(1.89, 365.24) * mm, "end": v(11.39, 365.24) * mm});
            skLineSegment(sketch, "E6.0.6.3", {"start": v(1.89, 375.35) * mm, "end": v(11.39, 375.35) * mm});
            skLineSegment(sketch, "E6.0.6.4", {"start": v(1.89, 375.35) * mm, "end": v(1.89, 365.24) * mm});
            skLineSegment(sketch, "E6.0.6.5", {"start": v(11.39, 375.35) * mm, "end": v(11.39, 365.24) * mm});
            skLineSegment(sketch, "E6.0.6.6", {"start": v(13.39, 375.35) * mm, "end": v(22.89, 375.35) * mm});
            skLineSegment(sketch, "E6.0.6.7", {"start": v(13.39, 375.35) * mm, "end": v(13.39, 365.24) * mm});
            skLineSegment(sketch, "E6.0.7.0", {"start": v(22.89, 363.24) * mm, "end": v(22.89, 353.13) * mm});
            skLineSegment(sketch, "E6.0.7.1", {"start": v(13.39, 353.13) * mm, "end": v(22.89, 353.13) * mm});
            skLineSegment(sketch, "E6.0.7.2", {"start": v(1.89, 353.13) * mm, "end": v(11.39, 353.13) * mm});
            skLineSegment(sketch, "E6.0.7.3", {"start": v(1.89, 363.24) * mm, "end": v(11.39, 363.24) * mm});
            skLineSegment(sketch, "E6.0.7.4", {"start": v(1.89, 363.24) * mm, "end": v(1.89, 353.13) * mm});
            skLineSegment(sketch, "E6.0.7.5", {"start": v(11.39, 363.24) * mm, "end": v(11.39, 353.13) * mm});
            skLineSegment(sketch, "E6.0.7.6", {"start": v(13.39, 363.24) * mm, "end": v(22.89, 363.24) * mm});
            skLineSegment(sketch, "E6.0.7.7", {"start": v(13.39, 363.24) * mm, "end": v(13.39, 353.13) * mm});
            skLineSegment(sketch, "E6.0.8.0", {"start": v(22.89, 351.13) * mm, "end": v(22.89, 341.02) * mm});
            skLineSegment(sketch, "E6.0.8.1", {"start": v(13.39, 341.02) * mm, "end": v(22.89, 341.02) * mm});
            skLineSegment(sketch, "E6.0.8.2", {"start": v(1.89, 341.02) * mm, "end": v(11.39, 341.02) * mm});
            skLineSegment(sketch, "E6.0.8.3", {"start": v(1.89, 351.13) * mm, "end": v(11.39, 351.13) * mm});
            skLineSegment(sketch, "E6.0.8.4", {"start": v(1.89, 351.13) * mm, "end": v(1.89, 341.02) * mm});
            skLineSegment(sketch, "E6.0.8.5", {"start": v(11.39, 351.13) * mm, "end": v(11.39, 341.02) * mm});
            skLineSegment(sketch, "E6.0.8.6", {"start": v(13.39, 351.13) * mm, "end": v(22.89, 351.13) * mm});
            skLineSegment(sketch, "E6.0.8.7", {"start": v(13.39, 351.13) * mm, "end": v(13.39, 341.02) * mm});
            skLineSegment(sketch, "E6.0.9.0", {"start": v(22.89, 339.02) * mm, "end": v(22.89, 328.92) * mm});
            skLineSegment(sketch, "E6.0.9.1", {"start": v(13.39, 328.92) * mm, "end": v(22.89, 328.92) * mm});
            skLineSegment(sketch, "E6.0.9.2", {"start": v(1.89, 328.92) * mm, "end": v(11.39, 328.92) * mm});
            skLineSegment(sketch, "E6.0.9.3", {"start": v(1.89, 339.02) * mm, "end": v(11.39, 339.02) * mm});
            skLineSegment(sketch, "E6.0.9.4", {"start": v(1.89, 339.02) * mm, "end": v(1.89, 328.92) * mm});
            skLineSegment(sketch, "E6.0.9.5", {"start": v(11.39, 339.02) * mm, "end": v(11.39, 328.92) * mm});
            skLineSegment(sketch, "E6.0.9.6", {"start": v(13.39, 339.02) * mm, "end": v(22.89, 339.02) * mm});
            skLineSegment(sketch, "E6.0.9.7", {"start": v(13.39, 339.02) * mm, "end": v(13.39, 328.92) * mm});
            skLineSegment(sketch, "E6.0.10.0", {"start": v(22.89, 326.92) * mm, "end": v(22.89, 316.8) * mm});
            skLineSegment(sketch, "E6.0.10.1", {"start": v(13.39, 316.8) * mm, "end": v(22.89, 316.8) * mm});
            skLineSegment(sketch, "E6.0.10.2", {"start": v(1.89, 316.8) * mm, "end": v(11.39, 316.8) * mm});
            skLineSegment(sketch, "E6.0.10.3", {"start": v(1.89, 326.92) * mm, "end": v(11.39, 326.92) * mm});
            skLineSegment(sketch, "E6.0.10.4", {"start": v(1.89, 326.92) * mm, "end": v(1.89, 316.8) * mm});
            skLineSegment(sketch, "E6.0.10.5", {"start": v(11.39, 326.92) * mm, "end": v(11.39, 316.8) * mm});
            skLineSegment(sketch, "E6.0.10.6", {"start": v(13.39, 326.92) * mm, "end": v(22.89, 326.92) * mm});
            skLineSegment(sketch, "E6.0.10.7", {"start": v(13.39, 326.92) * mm, "end": v(13.39, 316.8) * mm});
            skLineSegment(sketch, "E6.0.11.0", {"start": v(22.89, 314.8) * mm, "end": v(22.89, 304.7) * mm});
            skLineSegment(sketch, "E6.0.11.1", {"start": v(13.39, 304.7) * mm, "end": v(22.89, 304.7) * mm});
            skLineSegment(sketch, "E6.0.11.2", {"start": v(1.89, 304.7) * mm, "end": v(11.39, 304.7) * mm});
            skLineSegment(sketch, "E6.0.11.3", {"start": v(1.89, 314.8) * mm, "end": v(11.39, 314.8) * mm});
            skLineSegment(sketch, "E6.0.11.4", {"start": v(1.89, 314.8) * mm, "end": v(1.89, 304.7) * mm});
            skLineSegment(sketch, "E6.0.11.5", {"start": v(11.39, 314.8) * mm, "end": v(11.39, 304.7) * mm});
            skLineSegment(sketch, "E6.0.11.6", {"start": v(13.39, 314.8) * mm, "end": v(22.89, 314.8) * mm});
            skLineSegment(sketch, "E6.0.11.7", {"start": v(13.39, 314.8) * mm, "end": v(13.39, 304.7) * mm});
            skLineSegment(sketch, "E6.0.12.0", {"start": v(22.89, 302.7) * mm, "end": v(22.89, 292.6) * mm});
            skLineSegment(sketch, "E6.0.12.1", {"start": v(13.39, 292.6) * mm, "end": v(22.89, 292.6) * mm});
            skLineSegment(sketch, "E6.0.12.2", {"start": v(1.89, 292.6) * mm, "end": v(11.39, 292.6) * mm});
            skLineSegment(sketch, "E6.0.12.3", {"start": v(1.89, 302.7) * mm, "end": v(11.39, 302.7) * mm});
            skLineSegment(sketch, "E6.0.12.4", {"start": v(1.89, 302.7) * mm, "end": v(1.89, 292.6) * mm});
            skLineSegment(sketch, "E6.0.12.5", {"start": v(11.39, 302.7) * mm, "end": v(11.39, 292.6) * mm});
            skLineSegment(sketch, "E6.0.12.6", {"start": v(13.39, 302.7) * mm, "end": v(22.89, 302.7) * mm});
            skLineSegment(sketch, "E6.0.12.7", {"start": v(13.39, 302.7) * mm, "end": v(13.39, 292.6) * mm});
            skLineSegment(sketch, "E6.0.13.0", {"start": v(22.89, 290.6) * mm, "end": v(22.89, 280.48) * mm});
            skLineSegment(sketch, "E6.0.13.1", {"start": v(13.39, 280.48) * mm, "end": v(22.89, 280.48) * mm});
            skLineSegment(sketch, "E6.0.13.2", {"start": v(1.89, 280.48) * mm, "end": v(11.39, 280.48) * mm});
            skLineSegment(sketch, "E6.0.13.3", {"start": v(1.89, 290.6) * mm, "end": v(11.39, 290.6) * mm});
            skLineSegment(sketch, "E6.0.13.4", {"start": v(1.89, 290.6) * mm, "end": v(1.89, 280.48) * mm});
            skLineSegment(sketch, "E6.0.13.5", {"start": v(11.39, 290.6) * mm, "end": v(11.39, 280.48) * mm});
            skLineSegment(sketch, "E6.0.13.6", {"start": v(13.39, 290.6) * mm, "end": v(22.89, 290.6) * mm});
            skLineSegment(sketch, "E6.0.13.7", {"start": v(13.39, 290.6) * mm, "end": v(13.39, 280.48) * mm});
            skLineSegment(sketch, "E6.0.14.0", {"start": v(22.89, 278.48) * mm, "end": v(22.89, 268.38) * mm});
            skLineSegment(sketch, "E6.0.14.1", {"start": v(13.39, 268.38) * mm, "end": v(22.89, 268.38) * mm});
            skLineSegment(sketch, "E6.0.14.2", {"start": v(1.89, 268.38) * mm, "end": v(11.39, 268.38) * mm});
            skLineSegment(sketch, "E6.0.14.3", {"start": v(1.89, 278.48) * mm, "end": v(11.39, 278.48) * mm});
            skLineSegment(sketch, "E6.0.14.4", {"start": v(1.89, 278.48) * mm, "end": v(1.89, 268.38) * mm});
            skLineSegment(sketch, "E6.0.14.5", {"start": v(11.39, 278.48) * mm, "end": v(11.39, 268.38) * mm});
            skLineSegment(sketch, "E6.0.14.6", {"start": v(13.39, 278.48) * mm, "end": v(22.89, 278.48) * mm});
            skLineSegment(sketch, "E6.0.14.7", {"start": v(13.39, 278.48) * mm, "end": v(13.39, 268.38) * mm});
            skLineSegment(sketch, "E6.0.15.0", {"start": v(22.89, 266.38) * mm, "end": v(22.89, 256.27) * mm});
            skLineSegment(sketch, "E6.0.15.1", {"start": v(13.39, 256.27) * mm, "end": v(22.89, 256.27) * mm});
            skLineSegment(sketch, "E6.0.15.2", {"start": v(1.89, 256.27) * mm, "end": v(11.39, 256.27) * mm});
            skLineSegment(sketch, "E6.0.15.3", {"start": v(1.89, 266.38) * mm, "end": v(11.39, 266.38) * mm});
            skLineSegment(sketch, "E6.0.15.4", {"start": v(1.89, 266.38) * mm, "end": v(1.89, 256.27) * mm});
            skLineSegment(sketch, "E6.0.15.5", {"start": v(11.39, 266.38) * mm, "end": v(11.39, 256.27) * mm});
            skLineSegment(sketch, "E6.0.15.6", {"start": v(13.39, 266.38) * mm, "end": v(22.89, 266.38) * mm});
            skLineSegment(sketch, "E6.0.15.7", {"start": v(13.39, 266.38) * mm, "end": v(13.39, 256.27) * mm});
            skLineSegment(sketch, "E6.0.16.0", {"start": v(22.89, 254.27) * mm, "end": v(22.89, 244.16) * mm});
            skLineSegment(sketch, "E6.0.16.1", {"start": v(13.39, 244.16) * mm, "end": v(22.89, 244.16) * mm});
            skLineSegment(sketch, "E6.0.16.2", {"start": v(1.89, 244.16) * mm, "end": v(11.39, 244.16) * mm});
            skLineSegment(sketch, "E6.0.16.3", {"start": v(1.89, 254.27) * mm, "end": v(11.39, 254.27) * mm});
            skLineSegment(sketch, "E6.0.16.4", {"start": v(1.89, 254.27) * mm, "end": v(1.89, 244.16) * mm});
            skLineSegment(sketch, "E6.0.16.5", {"start": v(11.39, 254.27) * mm, "end": v(11.39, 244.16) * mm});
            skLineSegment(sketch, "E6.0.16.6", {"start": v(13.39, 254.27) * mm, "end": v(22.89, 254.27) * mm});
            skLineSegment(sketch, "E6.0.16.7", {"start": v(13.39, 254.27) * mm, "end": v(13.39, 244.16) * mm});
            skLineSegment(sketch, "E6.0.17.0", {"start": v(22.89, 242.16) * mm, "end": v(22.89, 232.05) * mm});
            skLineSegment(sketch, "E6.0.17.1", {"start": v(13.39, 232.05) * mm, "end": v(22.89, 232.05) * mm});
            skLineSegment(sketch, "E6.0.17.2", {"start": v(1.89, 232.05) * mm, "end": v(11.39, 232.05) * mm});
            skLineSegment(sketch, "E6.0.17.3", {"start": v(1.89, 242.16) * mm, "end": v(11.39, 242.16) * mm});
            skLineSegment(sketch, "E6.0.17.4", {"start": v(1.89, 242.16) * mm, "end": v(1.89, 232.05) * mm});
            skLineSegment(sketch, "E6.0.17.5", {"start": v(11.39, 242.16) * mm, "end": v(11.39, 232.05) * mm});
            skLineSegment(sketch, "E6.0.17.6", {"start": v(13.39, 242.16) * mm, "end": v(22.89, 242.16) * mm});
            skLineSegment(sketch, "E6.0.17.7", {"start": v(13.39, 242.16) * mm, "end": v(13.39, 232.05) * mm});
            skLineSegment(sketch, "E6.0.18.0", {"start": v(22.89, 230.05) * mm, "end": v(22.89, 219.94) * mm});
            skLineSegment(sketch, "E6.0.18.1", {"start": v(13.39, 219.94) * mm, "end": v(22.89, 219.94) * mm});
            skLineSegment(sketch, "E6.0.18.2", {"start": v(1.89, 219.94) * mm, "end": v(11.39, 219.94) * mm});
            skLineSegment(sketch, "E6.0.18.3", {"start": v(1.89, 230.05) * mm, "end": v(11.39, 230.05) * mm});
            skLineSegment(sketch, "E6.0.18.4", {"start": v(1.89, 230.05) * mm, "end": v(1.89, 219.94) * mm});
            skLineSegment(sketch, "E6.0.18.5", {"start": v(11.39, 230.05) * mm, "end": v(11.39, 219.94) * mm});
            skLineSegment(sketch, "E6.0.18.6", {"start": v(13.39, 230.05) * mm, "end": v(22.89, 230.05) * mm});
            skLineSegment(sketch, "E6.0.18.7", {"start": v(13.39, 230.05) * mm, "end": v(13.39, 219.94) * mm});
            skLineSegment(sketch, "E6.0.19.0", {"start": v(22.89, 217.94) * mm, "end": v(22.89, 207.84) * mm});
            skLineSegment(sketch, "E6.0.19.1", {"start": v(13.39, 207.84) * mm, "end": v(22.89, 207.84) * mm});
            skLineSegment(sketch, "E6.0.19.2", {"start": v(1.89, 207.84) * mm, "end": v(11.39, 207.84) * mm});
            skLineSegment(sketch, "E6.0.19.3", {"start": v(1.89, 217.94) * mm, "end": v(11.39, 217.94) * mm});
            skLineSegment(sketch, "E6.0.19.4", {"start": v(1.89, 217.94) * mm, "end": v(1.89, 207.84) * mm});
            skLineSegment(sketch, "E6.0.19.5", {"start": v(11.39, 217.94) * mm, "end": v(11.39, 207.84) * mm});
            skLineSegment(sketch, "E6.0.19.6", {"start": v(13.39, 217.94) * mm, "end": v(22.89, 217.94) * mm});
            skLineSegment(sketch, "E6.0.19.7", {"start": v(13.39, 217.94) * mm, "end": v(13.39, 207.84) * mm});
            skLineSegment(sketch, "E6.0.20.0", {"start": v(22.89, 205.84) * mm, "end": v(22.89, 195.73) * mm});
            skLineSegment(sketch, "E6.0.20.1", {"start": v(13.39, 195.73) * mm, "end": v(22.89, 195.73) * mm});
            skLineSegment(sketch, "E6.0.20.2", {"start": v(1.89, 195.73) * mm, "end": v(11.39, 195.73) * mm});
            skLineSegment(sketch, "E6.0.20.3", {"start": v(1.89, 205.84) * mm, "end": v(11.39, 205.84) * mm});
            skLineSegment(sketch, "E6.0.20.4", {"start": v(1.89, 205.84) * mm, "end": v(1.89, 195.73) * mm});
            skLineSegment(sketch, "E6.0.20.5", {"start": v(11.39, 205.84) * mm, "end": v(11.39, 195.73) * mm});
            skLineSegment(sketch, "E6.0.20.6", {"start": v(13.39, 205.84) * mm, "end": v(22.89, 205.84) * mm});
            skLineSegment(sketch, "E6.0.20.7", {"start": v(13.39, 205.84) * mm, "end": v(13.39, 195.73) * mm});
            skLineSegment(sketch, "E6.0.21.0", {"start": v(22.89, 193.73) * mm, "end": v(22.89, 183.62) * mm});
            skLineSegment(sketch, "E6.0.21.1", {"start": v(13.39, 183.62) * mm, "end": v(22.89, 183.62) * mm});
            skLineSegment(sketch, "E6.0.21.2", {"start": v(1.89, 183.62) * mm, "end": v(11.39, 183.62) * mm});
            skLineSegment(sketch, "E6.0.21.3", {"start": v(1.89, 193.73) * mm, "end": v(11.39, 193.73) * mm});
            skLineSegment(sketch, "E6.0.21.4", {"start": v(1.89, 193.73) * mm, "end": v(1.89, 183.62) * mm});
            skLineSegment(sketch, "E6.0.21.5", {"start": v(11.39, 193.73) * mm, "end": v(11.39, 183.62) * mm});
            skLineSegment(sketch, "E6.0.21.6", {"start": v(13.39, 193.73) * mm, "end": v(22.89, 193.73) * mm});
            skLineSegment(sketch, "E6.0.21.7", {"start": v(13.39, 193.73) * mm, "end": v(13.39, 183.62) * mm});
            skLineSegment(sketch, "E6.0.22.0", {"start": v(22.89, 181.62) * mm, "end": v(22.89, 171.51) * mm});
            skLineSegment(sketch, "E6.0.22.1", {"start": v(13.39, 171.51) * mm, "end": v(22.89, 171.51) * mm});
            skLineSegment(sketch, "E6.0.22.2", {"start": v(1.89, 171.51) * mm, "end": v(11.39, 171.51) * mm});
            skLineSegment(sketch, "E6.0.22.3", {"start": v(1.89, 181.62) * mm, "end": v(11.39, 181.62) * mm});
            skLineSegment(sketch, "E6.0.22.4", {"start": v(1.89, 181.62) * mm, "end": v(1.89, 171.51) * mm});
            skLineSegment(sketch, "E6.0.22.5", {"start": v(11.39, 181.62) * mm, "end": v(11.39, 171.51) * mm});
            skLineSegment(sketch, "E6.0.22.6", {"start": v(13.39, 181.62) * mm, "end": v(22.89, 181.62) * mm});
            skLineSegment(sketch, "E6.0.22.7", {"start": v(13.39, 181.62) * mm, "end": v(13.39, 171.51) * mm});
            skLineSegment(sketch, "E6.0.23.0", {"start": v(22.89, 169.51) * mm, "end": v(22.89, 159.4) * mm});
            skLineSegment(sketch, "E6.0.23.1", {"start": v(13.39, 159.4) * mm, "end": v(22.89, 159.4) * mm});
            skLineSegment(sketch, "E6.0.23.2", {"start": v(1.89, 159.4) * mm, "end": v(11.39, 159.4) * mm});
            skLineSegment(sketch, "E6.0.23.3", {"start": v(1.89, 169.51) * mm, "end": v(11.39, 169.51) * mm});
            skLineSegment(sketch, "E6.0.23.4", {"start": v(1.89, 169.51) * mm, "end": v(1.89, 159.4) * mm});
            skLineSegment(sketch, "E6.0.23.5", {"start": v(11.39, 169.51) * mm, "end": v(11.39, 159.4) * mm});
            skLineSegment(sketch, "E6.0.23.6", {"start": v(13.39, 169.51) * mm, "end": v(22.89, 169.51) * mm});
            skLineSegment(sketch, "E6.0.23.7", {"start": v(13.39, 169.51) * mm, "end": v(13.39, 159.4) * mm});
            skLineSegment(sketch, "E6.0.24.0", {"start": v(22.89, 157.4) * mm, "end": v(22.89, 147.3) * mm});
            skLineSegment(sketch, "E6.0.24.1", {"start": v(13.39, 147.3) * mm, "end": v(22.89, 147.3) * mm});
            skLineSegment(sketch, "E6.0.24.2", {"start": v(1.89, 147.3) * mm, "end": v(11.39, 147.3) * mm});
            skLineSegment(sketch, "E6.0.24.3", {"start": v(1.89, 157.4) * mm, "end": v(11.39, 157.4) * mm});
            skLineSegment(sketch, "E6.0.24.4", {"start": v(1.89, 157.4) * mm, "end": v(1.89, 147.3) * mm});
            skLineSegment(sketch, "E6.0.24.5", {"start": v(11.39, 157.4) * mm, "end": v(11.39, 147.3) * mm});
            skLineSegment(sketch, "E6.0.24.6", {"start": v(13.39, 157.4) * mm, "end": v(22.89, 157.4) * mm});
            skLineSegment(sketch, "E6.0.24.7", {"start": v(13.39, 157.4) * mm, "end": v(13.39, 147.3) * mm});
            skLineSegment(sketch, "E6.0.25.0", {"start": v(22.89, 145.3) * mm, "end": v(22.89, 135.19) * mm});
            skLineSegment(sketch, "E6.0.25.1", {"start": v(13.39, 135.19) * mm, "end": v(22.89, 135.19) * mm});
            skLineSegment(sketch, "E6.0.25.2", {"start": v(1.89, 135.19) * mm, "end": v(11.39, 135.19) * mm});
            skLineSegment(sketch, "E6.0.25.3", {"start": v(1.89, 145.3) * mm, "end": v(11.39, 145.3) * mm});
            skLineSegment(sketch, "E6.0.25.4", {"start": v(1.89, 145.3) * mm, "end": v(1.89, 135.19) * mm});
            skLineSegment(sketch, "E6.0.25.5", {"start": v(11.39, 145.3) * mm, "end": v(11.39, 135.19) * mm});
            skLineSegment(sketch, "E6.0.25.6", {"start": v(13.39, 145.3) * mm, "end": v(22.89, 145.3) * mm});
            skLineSegment(sketch, "E6.0.25.7", {"start": v(13.39, 145.3) * mm, "end": v(13.39, 135.19) * mm});
            skLineSegment(sketch, "E6.0.26.0", {"start": v(22.89, 133.19) * mm, "end": v(22.89, 123.08) * mm});
            skLineSegment(sketch, "E6.0.26.1", {"start": v(13.39, 123.08) * mm, "end": v(22.89, 123.08) * mm});
            skLineSegment(sketch, "E6.0.26.2", {"start": v(1.89, 123.08) * mm, "end": v(11.39, 123.08) * mm});
            skLineSegment(sketch, "E6.0.26.3", {"start": v(1.89, 133.19) * mm, "end": v(11.39, 133.19) * mm});
            skLineSegment(sketch, "E6.0.26.4", {"start": v(1.89, 133.19) * mm, "end": v(1.89, 123.08) * mm});
            skLineSegment(sketch, "E6.0.26.5", {"start": v(11.39, 133.19) * mm, "end": v(11.39, 123.08) * mm});
            skLineSegment(sketch, "E6.0.26.6", {"start": v(13.39, 133.19) * mm, "end": v(22.89, 133.19) * mm});
            skLineSegment(sketch, "E6.0.26.7", {"start": v(13.39, 133.19) * mm, "end": v(13.39, 123.08) * mm});
            skLineSegment(sketch, "E6.0.27.0", {"start": v(22.89, 121.08) * mm, "end": v(22.89, 110.97) * mm});
            skLineSegment(sketch, "E6.0.27.1", {"start": v(13.39, 110.97) * mm, "end": v(22.89, 110.97) * mm});
            skLineSegment(sketch, "E6.0.27.2", {"start": v(1.89, 110.97) * mm, "end": v(11.39, 110.97) * mm});
            skLineSegment(sketch, "E6.0.27.3", {"start": v(1.89, 121.08) * mm, "end": v(11.39, 121.08) * mm});
            skLineSegment(sketch, "E6.0.27.4", {"start": v(1.89, 121.08) * mm, "end": v(1.89, 110.97) * mm});
            skLineSegment(sketch, "E6.0.27.5", {"start": v(11.39, 121.08) * mm, "end": v(11.39, 110.97) * mm});
            skLineSegment(sketch, "E6.0.27.6", {"start": v(13.39, 121.08) * mm, "end": v(22.89, 121.08) * mm});
            skLineSegment(sketch, "E6.0.27.7", {"start": v(13.39, 121.08) * mm, "end": v(13.39, 110.97) * mm});
            skLineSegment(sketch, "E6.0.28.0", {"start": v(22.89, 108.97) * mm, "end": v(22.89, 98.86) * mm});
            skLineSegment(sketch, "E6.0.28.1", {"start": v(13.39, 98.86) * mm, "end": v(22.89, 98.86) * mm});
            skLineSegment(sketch, "E6.0.28.2", {"start": v(1.89, 98.86) * mm, "end": v(11.39, 98.86) * mm});
            skLineSegment(sketch, "E6.0.28.3", {"start": v(1.89, 108.97) * mm, "end": v(11.39, 108.97) * mm});
            skLineSegment(sketch, "E6.0.28.4", {"start": v(1.89, 108.97) * mm, "end": v(1.89, 98.86) * mm});
            skLineSegment(sketch, "E6.0.28.5", {"start": v(11.39, 108.97) * mm, "end": v(11.39, 98.86) * mm});
            skLineSegment(sketch, "E6.0.28.6", {"start": v(13.39, 108.97) * mm, "end": v(22.89, 108.97) * mm});
            skLineSegment(sketch, "E6.0.28.7", {"start": v(13.39, 108.97) * mm, "end": v(13.39, 98.86) * mm});
            skLineSegment(sketch, "E6.0.29.0", {"start": v(22.89, 96.86) * mm, "end": v(22.89, 86.76) * mm});
            skLineSegment(sketch, "E6.0.29.1", {"start": v(13.39, 86.76) * mm, "end": v(22.89, 86.76) * mm});
            skLineSegment(sketch, "E6.0.29.2", {"start": v(1.89, 86.76) * mm, "end": v(11.39, 86.76) * mm});
            skLineSegment(sketch, "E6.0.29.3", {"start": v(1.89, 96.86) * mm, "end": v(11.39, 96.86) * mm});
            skLineSegment(sketch, "E6.0.29.4", {"start": v(1.89, 96.86) * mm, "end": v(1.89, 86.76) * mm});
            skLineSegment(sketch, "E6.0.29.5", {"start": v(11.39, 96.86) * mm, "end": v(11.39, 86.76) * mm});
            skLineSegment(sketch, "E6.0.29.6", {"start": v(13.39, 96.86) * mm, "end": v(22.89, 96.86) * mm});
            skLineSegment(sketch, "E6.0.29.7", {"start": v(13.39, 96.86) * mm, "end": v(13.39, 86.76) * mm});
            skLineSegment(sketch, "E6.0.30.0", {"start": v(22.89, 84.76) * mm, "end": v(22.89, 74.65) * mm});
            skLineSegment(sketch, "E6.0.30.1", {"start": v(13.39, 74.65) * mm, "end": v(22.89, 74.65) * mm});
            skLineSegment(sketch, "E6.0.30.2", {"start": v(1.89, 74.65) * mm, "end": v(11.39, 74.65) * mm});
            skLineSegment(sketch, "E6.0.30.3", {"start": v(1.89, 84.76) * mm, "end": v(11.39, 84.76) * mm});
            skLineSegment(sketch, "E6.0.30.4", {"start": v(1.89, 84.76) * mm, "end": v(1.89, 74.65) * mm});
            skLineSegment(sketch, "E6.0.30.5", {"start": v(11.39, 84.76) * mm, "end": v(11.39, 74.65) * mm});
            skLineSegment(sketch, "E6.0.30.6", {"start": v(13.39, 84.76) * mm, "end": v(22.89, 84.76) * mm});
            skLineSegment(sketch, "E6.0.30.7", {"start": v(13.39, 84.76) * mm, "end": v(13.39, 74.65) * mm});
            skLineSegment(sketch, "E6.0.31.0", {"start": v(22.89, 72.65) * mm, "end": v(22.89, 62.54) * mm});
            skLineSegment(sketch, "E6.0.31.1", {"start": v(13.39, 62.54) * mm, "end": v(22.89, 62.54) * mm});
            skLineSegment(sketch, "E6.0.31.2", {"start": v(1.89, 62.54) * mm, "end": v(11.39, 62.54) * mm});
            skLineSegment(sketch, "E6.0.31.3", {"start": v(1.89, 72.65) * mm, "end": v(11.39, 72.65) * mm});
            skLineSegment(sketch, "E6.0.31.4", {"start": v(1.89, 72.65) * mm, "end": v(1.89, 62.54) * mm});
            skLineSegment(sketch, "E6.0.31.5", {"start": v(11.39, 72.65) * mm, "end": v(11.39, 62.54) * mm});
            skLineSegment(sketch, "E6.0.31.6", {"start": v(13.39, 72.65) * mm, "end": v(22.89, 72.65) * mm});
            skLineSegment(sketch, "E6.0.31.7", {"start": v(13.39, 72.65) * mm, "end": v(13.39, 62.54) * mm});
            skLineSegment(sketch, "E6.0.32.0", {"start": v(22.89, 60.54) * mm, "end": v(22.89, 50.43) * mm});
            skLineSegment(sketch, "E6.0.32.1", {"start": v(13.39, 50.43) * mm, "end": v(22.89, 50.43) * mm});
            skLineSegment(sketch, "E6.0.32.2", {"start": v(1.89, 50.43) * mm, "end": v(11.39, 50.43) * mm});
            skLineSegment(sketch, "E6.0.32.3", {"start": v(1.89, 60.54) * mm, "end": v(11.39, 60.54) * mm});
            skLineSegment(sketch, "E6.0.32.4", {"start": v(1.89, 60.54) * mm, "end": v(1.89, 50.43) * mm});
            skLineSegment(sketch, "E6.0.32.5", {"start": v(11.39, 60.54) * mm, "end": v(11.39, 50.43) * mm});
            skLineSegment(sketch, "E6.0.32.6", {"start": v(13.39, 60.54) * mm, "end": v(22.89, 60.54) * mm});
            skLineSegment(sketch, "E6.0.32.7", {"start": v(13.39, 60.54) * mm, "end": v(13.39, 50.43) * mm});
            skLineSegment(sketch, "E6.0.33.0", {"start": v(22.89, 48.43) * mm, "end": v(22.89, 38.32) * mm});
            skLineSegment(sketch, "E6.0.33.1", {"start": v(13.39, 38.32) * mm, "end": v(22.89, 38.32) * mm});
            skLineSegment(sketch, "E6.0.33.2", {"start": v(1.89, 38.32) * mm, "end": v(11.39, 38.32) * mm});
            skLineSegment(sketch, "E6.0.33.3", {"start": v(1.89, 48.43) * mm, "end": v(11.39, 48.43) * mm});
            skLineSegment(sketch, "E6.0.33.4", {"start": v(1.89, 48.43) * mm, "end": v(1.89, 38.32) * mm});
            skLineSegment(sketch, "E6.0.33.5", {"start": v(11.39, 48.43) * mm, "end": v(11.39, 38.32) * mm});
            skLineSegment(sketch, "E6.0.33.6", {"start": v(13.39, 48.43) * mm, "end": v(22.89, 48.43) * mm});
            skLineSegment(sketch, "E6.0.33.7", {"start": v(13.39, 48.43) * mm, "end": v(13.39, 38.32) * mm});
            skLineSegment(sketch, "E6.0.34.0", {"start": v(22.89, 36.32) * mm, "end": v(22.89, 26.22) * mm});
            skLineSegment(sketch, "E6.0.34.1", {"start": v(13.39, 26.22) * mm, "end": v(22.89, 26.22) * mm});
            skLineSegment(sketch, "E6.0.34.2", {"start": v(1.89, 26.22) * mm, "end": v(11.39, 26.22) * mm});
            skLineSegment(sketch, "E6.0.34.3", {"start": v(1.89, 36.32) * mm, "end": v(11.39, 36.32) * mm});
            skLineSegment(sketch, "E6.0.34.4", {"start": v(1.89, 36.32) * mm, "end": v(1.89, 26.22) * mm});
            skLineSegment(sketch, "E6.0.34.5", {"start": v(11.39, 36.32) * mm, "end": v(11.39, 26.22) * mm});
            skLineSegment(sketch, "E6.0.34.6", {"start": v(13.39, 36.32) * mm, "end": v(22.89, 36.32) * mm});
            skLineSegment(sketch, "E6.0.34.7", {"start": v(13.39, 36.32) * mm, "end": v(13.39, 26.22) * mm});
            skLineSegment(sketch, "E6.0.35.0", {"start": v(22.89, 24.22) * mm, "end": v(22.89, 14.1) * mm});
            skLineSegment(sketch, "E6.0.35.1", {"start": v(13.39, 14.1) * mm, "end": v(22.89, 14.1) * mm});
            skLineSegment(sketch, "E6.0.35.2", {"start": v(1.89, 14.1) * mm, "end": v(11.39, 14.1) * mm});
            skLineSegment(sketch, "E6.0.35.3", {"start": v(1.89, 24.22) * mm, "end": v(11.39, 24.22) * mm});
            skLineSegment(sketch, "E6.0.35.4", {"start": v(1.89, 24.22) * mm, "end": v(1.89, 14.1) * mm});
            skLineSegment(sketch, "E6.0.35.5", {"start": v(11.39, 24.22) * mm, "end": v(11.39, 14.1) * mm});
            skLineSegment(sketch, "E6.0.35.6", {"start": v(13.39, 24.22) * mm, "end": v(22.89, 24.22) * mm});
            skLineSegment(sketch, "E6.0.35.7", {"start": v(13.39, 24.22) * mm, "end": v(13.39, 14.1) * mm});
            skLineSegment(sketch, "E6.0.36.0", {"start": v(22.89, 12.1) * mm, "end": v(22.89, 2) * mm});
            skLineSegment(sketch, "E6.0.36.1", {"start": v(13.39, 2) * mm, "end": v(22.89, 2) * mm});
            skLineSegment(sketch, "E6.0.36.2", {"start": v(1.89, 2) * mm, "end": v(11.39, 2) * mm});
            skLineSegment(sketch, "E6.0.36.3", {"start": v(1.89, 12.1) * mm, "end": v(11.39, 12.1) * mm});
            skLineSegment(sketch, "E6.0.36.4", {"start": v(1.89, 12.1) * mm, "end": v(1.89, 2) * mm});
            skLineSegment(sketch, "E6.0.36.5", {"start": v(11.39, 12.1) * mm, "end": v(11.39, 2) * mm});
            skLineSegment(sketch, "E6.0.36.6", {"start": v(13.39, 12.1) * mm, "end": v(22.89, 12.1) * mm});
            skLineSegment(sketch, "E6.0.36.7", {"start": v(13.39, 12.1) * mm, "end": v(13.39, 2) * mm});
            skLineSegment(sketch, "E6.direction1", {"start": v(22.89, 437.89) * mm, "end": v(47.89, 437.89) * mm, "construction": true});
            skLineSegment(sketch, "E6.direction2", {"start": v(22.89, 437.89) * mm, "end": v(22.89, 425.78) * mm, "construction": true});
            skSolve(sketch);
        }
        {
            var Q0;
            Q0 = qSketchRegion(id + "F4", true);
            extrude(context, id + "F5", {"entities" : qUnion([Q0]), "operationType" : NewBodyOperationType.REMOVE, "oppositeDirection" : true, "depth" : 4 * mm});
        }
    });
